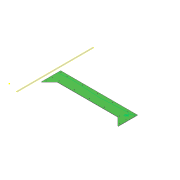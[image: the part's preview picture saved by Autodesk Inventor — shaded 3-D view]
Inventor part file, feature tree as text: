
AUTODESK INVENTOR PART (.ipt)
format: ipt  version: 2017 (Build 210142000, 142)  size: 1,242,112 bytes
history: native  units: mm
features: sketch x3, other x3, plane x1, extrude x1, hole x1, projected_geometry x1
ambient origin geometry x8: Origin, YZ Plane, XZ Plane, XY Plane, X Axis, Y Axis, Z Axis, Center Point
bodies: Solid1 (feature_tree)
feature tree (10):
  plane  "Work Plane1"
  extrude  "Extrusion1"  [1 undecoded]
  sketch  "Sketch2"  dims[d2=5.2mm d3=6.0mm d4=4.0mm d5=2.0mm d6=90.0deg d7=8.0mm d8=20.594885mm]
  hole  "Hole1"  [1 undecoded]
  sketch  "Sketch1"  dims[d0=3.0mm d1=0.0mm]
  sketch  "Sketch3"
  projected_geometry  "Projected Loop1"
  other  "<userpath>\OneDrive\Inventor\Beast 3D Printer\Main assembly Test.iam"
  other  "Main assembly Test.iam"
  other  "3030 600mm:6"
note: 2 required parameter values undecoded (feature->parameter linkage not recoverable at this tier; creation-order binding heuristic only, values carry confidence <= 0.55)
